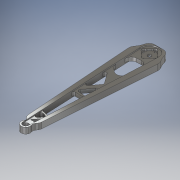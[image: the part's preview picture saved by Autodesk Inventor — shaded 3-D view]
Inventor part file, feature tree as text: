
AUTODESK INVENTOR PART (.ipt)
format: ipt  version: 2019.4 (Build 234330000, 330)  size: 656,896 bytes
history: native  units: mm
features: fillet x13, extrude x9, plane x8, sketch x8, other x2, pattern_circular x1, mirror x1
ambient origin geometry x8: Origin, YZ Plane, XZ Plane, XY Plane, X Axis, Y Axis, Z Axis, Center Point
bodies: Solid1 (feature_tree)
feature tree (42):
  other  "Delta_Arm"
  plane  "Work Plane6"
  plane  "Work Plane5"
  plane  "Work Plane7"
  plane  "Work Plane4"
  plane  "Work Plane1"
  plane  "Work Plane3"
  plane  "Work Plane2"
  extrude  "Extrusion8"  Depth=50.0mm
  extrude  "Extrusion9"  Depth=210.0mm
  extrude  "Extrusion11"  Depth=6.0mm
  plane  "Work Plane8"
  extrude  "Extrusion13"  Depth=10.0mm TaperAngle=0.0deg
  pattern_circular  "Circular Pattern1"  Count=21  [1 undecoded]
  extrude  "Extrusion14"  Depth=5.0mm TaperAngle=0.0deg
  mirror  "Mirror3"
  extrude  "Extrusion15"  Depth=3.0mm
  extrude  "Extrusion16"  Depth=40.0mm TaperAngle=360.0deg
  extrude  "Extrusion17"  Depth=10.0mm
  fillet  "Fillet4"  Radius=15.0mm
  fillet  "Fillet5"  Radius=2.0mm
  fillet  "Fillet6"  Radius=15.0mm
  fillet  "Fillet7"  Radius=20.0mm
  fillet  "Fillet8"  Radius=20.0mm
  fillet  "Fillet9"  Radius=6.0mm
  fillet  "Fillet10"  Radius=6.0mm
  fillet  "Fillet11"  Radius=30.0mm
  fillet  "Fillet12"  Radius=40.0mm
  fillet  "Fillet13"  Radius=10.0mm
  fillet  "Fillet14"  Radius=10.0mm
  fillet  "Fillet15"  Radius=3.0mm
  fillet  "Fillet16"  Radius=3.0mm
  extrude  "Extrusion18"  Depth=3.0mm
  sketch  "Sketch10"  dims[d0=20.0mm d2=50.0mm]
  sketch  "Sketch13"  dims[d44=5.0mm d50=210.0mm d51=210.0mm]
  sketch  "Sketch15"  dims[d52=10.0mm d53=0.0mm d54=6.0mm]
  sketch  "Sketch16"  dims[d55=6.0mm d56=10.0mm d57=0.0mm d63=210.0mm]
  sketch  "Sketch17"  dims[d64=25.0mm d65=5.0mm d66=0.0mm]
  sketch  "Sketch18"  dims[d70=-5.0mm d71=3.0mm]
  sketch  "Sketch19"  dims[d72=10.0mm d73=0.0mm d74=40.0mm d75=360.0deg]
  sketch  "Sketch20"  dims[d77=30.0mm d78=10.0mm d79=15.0mm d81=2.0mm d82=0.0mm d83=15.0mm d84=20.0mm d85=20.0mm d86=0.0mm d87=6.0mm d88=0.0mm d89=6.0mm d90=0.0mm d91=30.0mm d92=40.0mm d93=10.0mm d94=10.0mm d95=3.0mm d96=3.0mm d97=3.0mm d98=7.0mm d99=7.0mm d100=10.0mm d101=3.0mm d102=5.0mm d103=1.0mm d104=10.0mm d105=10.0mm d106=0.0mm]
  other  "MeshFeature1"
note: 1 required parameter value undecoded (feature->parameter linkage not recoverable at this tier; creation-order binding heuristic only, values carry confidence <= 0.55)
